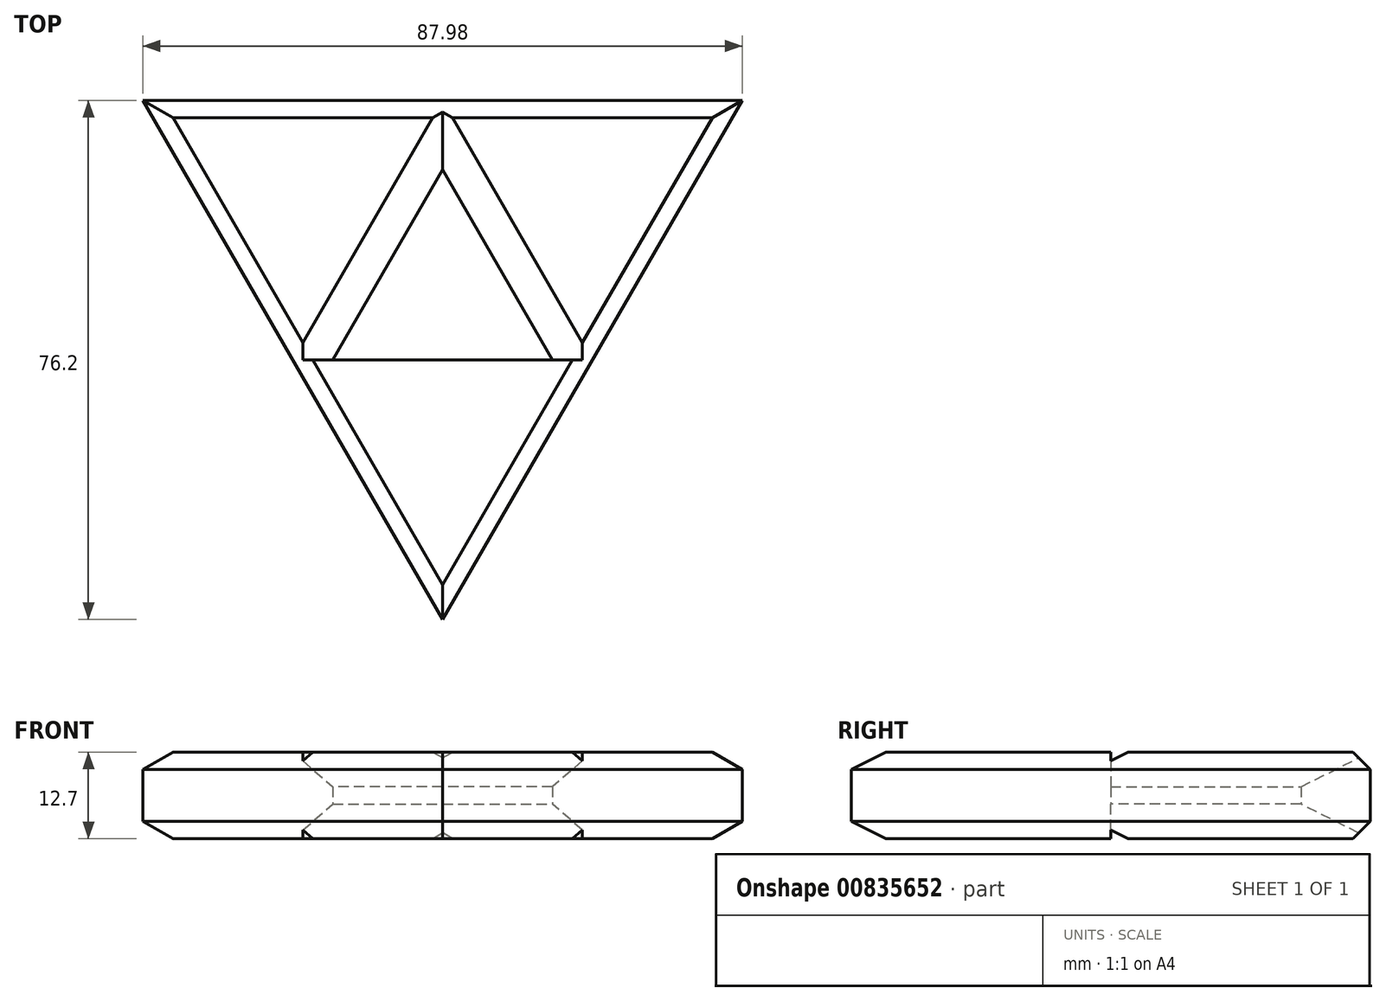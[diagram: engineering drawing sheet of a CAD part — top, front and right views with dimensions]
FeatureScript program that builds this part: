
annotation { "Feature Type Name" : "Feature", "Feature Type Description" : "" }
export const myFeature = defineFeature(function(context is Context, id is Id, definition is map)
    precondition{}
    {
        {
            var Q0;
            Q0=qCreatedBy(makeId("Top.planeOp"),FACE);
            var sketch = newSketch(context, id + "F0", { "sketchPlane" : qUnion([Q0])});
            skCircle(sketch, "E0.cCircle", {"center": v(0, 0) * mm, "radius": 25.4 * mm, "construction": true});
            skLineSegment(sketch, "E0.0", {"start": v(0, 25.4) * mm, "end": v(22, -12.7) * mm});
            skLineSegment(sketch, "E0.1", {"start": v(22, -12.7) * mm, "end": v(-22, -12.7) * mm});
            skLineSegment(sketch, "E0.2", {"start": v(-22, -12.7) * mm, "end": v(0, 25.4) * mm});
            skLineSegment(sketch, "E1", {"start": v(-11, 6.35) * mm, "end": v(-44, 25.4) * mm, "construction": true});
            skLineSegment(sketch, "E2", {"start": v(11, 6.35) * mm, "end": v(44, 25.4) * mm, "construction": true});
            skLineSegment(sketch, "E3", {"start": v(0, -12.7) * mm, "end": v(0, -50.8) * mm, "construction": true});
            skCircle(sketch, "E4.cCircle", {"center": v(-22, 12.7) * mm, "radius": 25.4 * mm, "construction": true});
            skLineSegment(sketch, "E4.0", {"start": v(-44, 25.4) * mm, "end": v(0, 25.4) * mm});
            skLineSegment(sketch, "E4.1", {"start": v(0, 25.4) * mm, "end": v(-22, -12.7) * mm});
            skLineSegment(sketch, "E4.2", {"start": v(-22, -12.7) * mm, "end": v(-44, 25.4) * mm});
            skCircle(sketch, "E5.cCircle", {"center": v(22, 12.7) * mm, "radius": 25.4 * mm, "construction": true});
            skLineSegment(sketch, "E5.0", {"start": v(44, 25.4) * mm, "end": v(22, -12.7) * mm});
            skLineSegment(sketch, "E5.1", {"start": v(22, -12.7) * mm, "end": v(0, 25.4) * mm});
            skLineSegment(sketch, "E5.2", {"start": v(0, 25.4) * mm, "end": v(44, 25.4) * mm});
            skCircle(sketch, "E6.cCircle", {"center": v(0, -25.4) * mm, "radius": 25.4 * mm, "construction": true});
            skLineSegment(sketch, "E6.0", {"start": v(0, -50.8) * mm, "end": v(-22, -12.7) * mm});
            skLineSegment(sketch, "E6.1", {"start": v(-22, -12.7) * mm, "end": v(22, -12.7) * mm});
            skLineSegment(sketch, "E6.2", {"start": v(22, -12.7) * mm, "end": v(0, -50.8) * mm});
            skLineSegment(sketch, "E7", {"start": v(-2.93, 20.32) * mm, "end": v(16.13, -12.7) * mm});
            skPoint(sketch, "E8", {"position": v(6.6, 3.81) * mm});
            skLineSegment(sketch, "E9", {"start": v(2.93, 20.32) * mm, "end": v(-16.13, -12.7) * mm});
            skLineSegment(sketch, "E10", {"start": v(-19.06, -7.62) * mm, "end": v(19.06, -7.62) * mm});
            skPoint(sketch, "E11", {"position": v(-6.6, 3.81) * mm});
            skPoint(sketch, "E12", {"position": v(0, -7.62) * mm});
            skSolve(sketch);
        }
        {
            var Q0;
            Q0=makeQuery(id+"F0.imprint","IMPRINT",FACE,{"disambiguationData":[TD([[makeQuery(id+"F0.imprint","IMPRINT",EDGE,{"derivedFrom":sQuery(id+"F0.wireOp",EDGE,"E4.0")}),-1.0]])]});
            var Q1;
            Q1=makeQuery(id+"F0.imprint","IMPRINT",FACE,{"disambiguationData":[TD([[makeQuery(id+"F0.imprint","IMPRINT",EDGE,{"derivedFrom":sQuery(id+"F0.wireOp",EDGE,"E6.0")}),-1.0]])]});
            var Q2;
            Q2=makeQuery(id+"F0.imprint","IMPRINT",FACE,{"disambiguationData":[TD([[makeQuery(id+"F0.imprint","IMPRINT",EDGE,{"derivedFrom":sQuery(id+"F0.wireOp",EDGE,"E5.0")}),-1.0]])]});
            var Q3;
            {var subQ0=sQuery(id+"F0.wireOp",EDGE,"E6.1");var subQ5=sQuery(id+"F0.wireOp",EDGE,"E9");var subQ6=makeQuery(id+"F0.imprint","INTERSECT",VERTEX,{"derivedFrom":[subQ0,subQ5]});Q3=makeQuery(id+"F0.imprint","IMPRINT",FACE,{"disambiguationData":[TD([[makeQuery(id+"F0.imprint","IMPRINT",EDGE,{"disambiguationData":[TD([[subQ6,1.0]])],"derivedFrom":subQ5}),-1.0]])]});}
            var Q4;
            {var subQ0=sQuery(id+"F0.wireOp",EDGE,"E7");var subQ1=sQuery(id+"F0.wireOp",EDGE,"E6.1");var subQ2=makeQuery(id+"F0.imprint","INTERSECT",VERTEX,{"derivedFrom":[subQ1,subQ0]});Q4=makeQuery(id+"F0.imprint","IMPRINT",FACE,{"disambiguationData":[TD([[makeQuery(id+"F0.imprint","IMPRINT",EDGE,{"disambiguationData":[TD([[subQ2,1.0]])],"derivedFrom":subQ1}),1.0]])]});}
            var Q5;
            {var subQ0=sQuery(id+"F0.wireOp",EDGE,"E6.1");var subQ5=sQuery(id+"F0.wireOp",EDGE,"E7");var subQ6=makeQuery(id+"F0.imprint","INTERSECT",VERTEX,{"derivedFrom":[subQ0,subQ5]});Q5=makeQuery(id+"F0.imprint","IMPRINT",FACE,{"disambiguationData":[TD([[makeQuery(id+"F0.imprint","IMPRINT",EDGE,{"disambiguationData":[TD([[subQ6,1.0]])],"derivedFrom":subQ5}),1.0]])]});}
            var Q6;
            {var subQ0=sQuery(id+"F0.wireOp",EDGE,"E9");var subQ1=sQuery(id+"F0.wireOp",EDGE,"E5.1");var subQ2=makeQuery(id+"F0.imprint","INTERSECT",VERTEX,{"derivedFrom":[subQ1,subQ0]});Q6=makeQuery(id+"F0.imprint","IMPRINT",FACE,{"disambiguationData":[TD([[makeQuery(id+"F0.imprint","IMPRINT",EDGE,{"disambiguationData":[TD([[subQ2,1.0]])],"derivedFrom":subQ1}),1.0]])]});}
            var Q7;
            {var subQ1=sQuery(id+"F0.wireOp",EDGE,"E4.1");var subQ3=sQuery(id+"F0.wireOp",EDGE,"E7");var subQ4=makeQuery(id+"F0.imprint","INTERSECT",VERTEX,{"derivedFrom":[subQ1,subQ3]});Q7=makeQuery(id+"F0.imprint","IMPRINT",FACE,{"disambiguationData":[TD([[makeQuery(id+"F0.imprint","IMPRINT",EDGE,{"disambiguationData":[TD([[subQ4,-1.0]])],"derivedFrom":subQ3}),1.0]])]});}
            var Q8;
            {var subQ0=sQuery(id+"F0.wireOp",EDGE,"E7");var subQ1=sQuery(id+"F0.wireOp",EDGE,"E4.1");var subQ2=makeQuery(id+"F0.imprint","INTERSECT",VERTEX,{"derivedFrom":[subQ1,subQ0]});Q8=makeQuery(id+"F0.imprint","IMPRINT",FACE,{"disambiguationData":[TD([[makeQuery(id+"F0.imprint","IMPRINT",EDGE,{"disambiguationData":[TD([[subQ2,-1.0]])],"derivedFrom":subQ1}),1.0]])]});}
            extrude(context, id + "F1", {"entities" : qUnion([Q0, Q1, Q2, Q3, Q4, Q5, Q6, Q7, Q8]), "depth" : 12.7 * mm, "offsetDistance" : 25.4 * mm});
        }
        {
            var Q0;
            Q0=makeQuery(id+"F1.opExtrude","CAP_EDGE",EDGE,{"disambiguationData":[OSD([sQuery(id+"F0.wireOp",EDGE,"E7")])],"isStart":false});
            var Q1;
            Q1=makeQuery(id+"F1.opExtrude","CAP_EDGE",EDGE,{"disambiguationData":[OSD([sQuery(id+"F0.wireOp",EDGE,"E9")])],"isStart":false});
            var Q2;
            Q2=makeQuery(id+"F1.opExtrude","CAP_EDGE",EDGE,{"disambiguationData":[OSD([sQuery(id+"F0.wireOp",EDGE,"E10")])],"isStart":false});
            var Q3;
            Q3=makeQuery(id+"F1.opExtrude","CAP_EDGE",EDGE,{"disambiguationData":[OSD([sQuery(id+"F0.wireOp",EDGE,"E7")])],"isStart":true});
            var Q4;
            Q4=makeQuery(id+"F1.opExtrude","CAP_EDGE",EDGE,{"disambiguationData":[OSD([sQuery(id+"F0.wireOp",EDGE,"E10")])],"isStart":true});
            var Q5;
            Q5=makeQuery(id+"F1.opExtrude","CAP_EDGE",EDGE,{"disambiguationData":[OSD([sQuery(id+"F0.wireOp",EDGE,"E9")])],"isStart":true});
            chamfer(context, id + "F2", {"entities" : qUnion([Q0, Q1, Q2, Q3, Q4, Q5]), "width" : 5.08 * mm, "tangentPropagation" : true});
        }
        {
            var Q0;
            Q0=makeQuery(id+"F1.opExtrude","CAP_EDGE",EDGE,{"disambiguationData":[OSD([sQuery(id+"F0.wireOp",EDGE,"E4.2"),sQuery(id+"F0.wireOp",EDGE,"E6.0")])],"isStart":false});
            var Q1;
            Q1=makeQuery(id+"F1.opExtrude","CAP_EDGE",EDGE,{"disambiguationData":[OSD([sQuery(id+"F0.wireOp",EDGE,"E5.0"),sQuery(id+"F0.wireOp",EDGE,"E6.2")])],"isStart":false});
            var Q2;
            Q2=makeQuery(id+"F1.opExtrude","CAP_EDGE",EDGE,{"disambiguationData":[OSD([sQuery(id+"F0.wireOp",EDGE,"E4.0"),sQuery(id+"F0.wireOp",EDGE,"E5.2")])],"isStart":false});
            var Q3;
            Q3=makeQuery(id+"F1.opExtrude","CAP_EDGE",EDGE,{"disambiguationData":[OSD([sQuery(id+"F0.wireOp",EDGE,"E5.0"),sQuery(id+"F0.wireOp",EDGE,"E6.2")])],"isStart":true});
            var Q4;
            Q4=makeQuery(id+"F1.opExtrude","CAP_EDGE",EDGE,{"disambiguationData":[OSD([sQuery(id+"F0.wireOp",EDGE,"E4.2"),sQuery(id+"F0.wireOp",EDGE,"E6.0")])],"isStart":true});
            var Q5;
            Q5=makeQuery(id+"F1.opExtrude","CAP_EDGE",EDGE,{"disambiguationData":[OSD([sQuery(id+"F0.wireOp",EDGE,"E4.0"),sQuery(id+"F0.wireOp",EDGE,"E5.2")])],"isStart":true});
            chamfer(context, id + "F3", {"entities" : qUnion([Q0, Q1, Q2, Q3, Q4, Q5]), "width" : 2.54 * mm, "tangentPropagation" : true});
        }
    });
